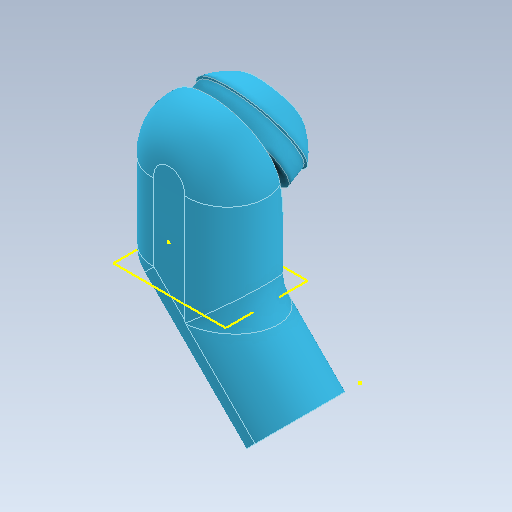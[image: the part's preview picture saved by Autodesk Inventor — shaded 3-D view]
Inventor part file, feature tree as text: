
AUTODESK INVENTOR PART (.ipt)
format: ipt  version: 2021 (Build 250183000, 183)  size: 366,080 bytes
history: native  units: mm
features: sketch x14, delete_face x7, other x4, extrude x3, mirror x1
ambient origin geometry x8: Origin, YZ Plane, XZ Plane, XY Plane, X Axis, Y Axis, Z Axis, Center Point
bodies: Solid1 (feature_tree), Solid2 (feature_tree)
feature tree (29):
  other  "toy hand part.ipt"
  sketch  "Sketch18"
  sketch  "Sketch19"
  extrude  "Extrusion1"  Depth=3.0mm
  extrude  "Extrusion2"  Depth=3.0mm
  extrude  "Extrusion3"  Depth=10.0mm
  delete_face  "Delete Face1"
  delete_face  "Delete Face2"
  delete_face  "Delete Face3"
  mirror  "Mirror1"
  delete_face  "Delete Face4"
  delete_face  "Delete Face5"
  delete_face  "Delete Face6"
  delete_face  "Delete Face7"
  other  "Solid2::toy hand part.ipt"
  other  "Solid3::toy hand part.ipt"
  other  "TaggingFeature1"
  sketch  "Sketch2"  dims[d0=30.0mm d1=3.0mm]
  sketch  "Sketch3"  dims[d2=3.0mm d3=3.0mm]
  sketch  "Sketch5"  dims[d4=10.0mm d5=0.698132mm d6=10.0mm d7=0.698132mm]
  sketch  "Sketch6"  dims[d8=3.0mm]
  sketch  "Sketch9"  dims[d9=7.5mm d10=0.698132mm]
  sketch  "Sketch15"
  sketch  "Sketch16"
  sketch  "Sketch17"
  sketch  "Sketch22"
  sketch  "Sketch25"
  sketch  "Sketch26"
  sketch  "Sketch20"
